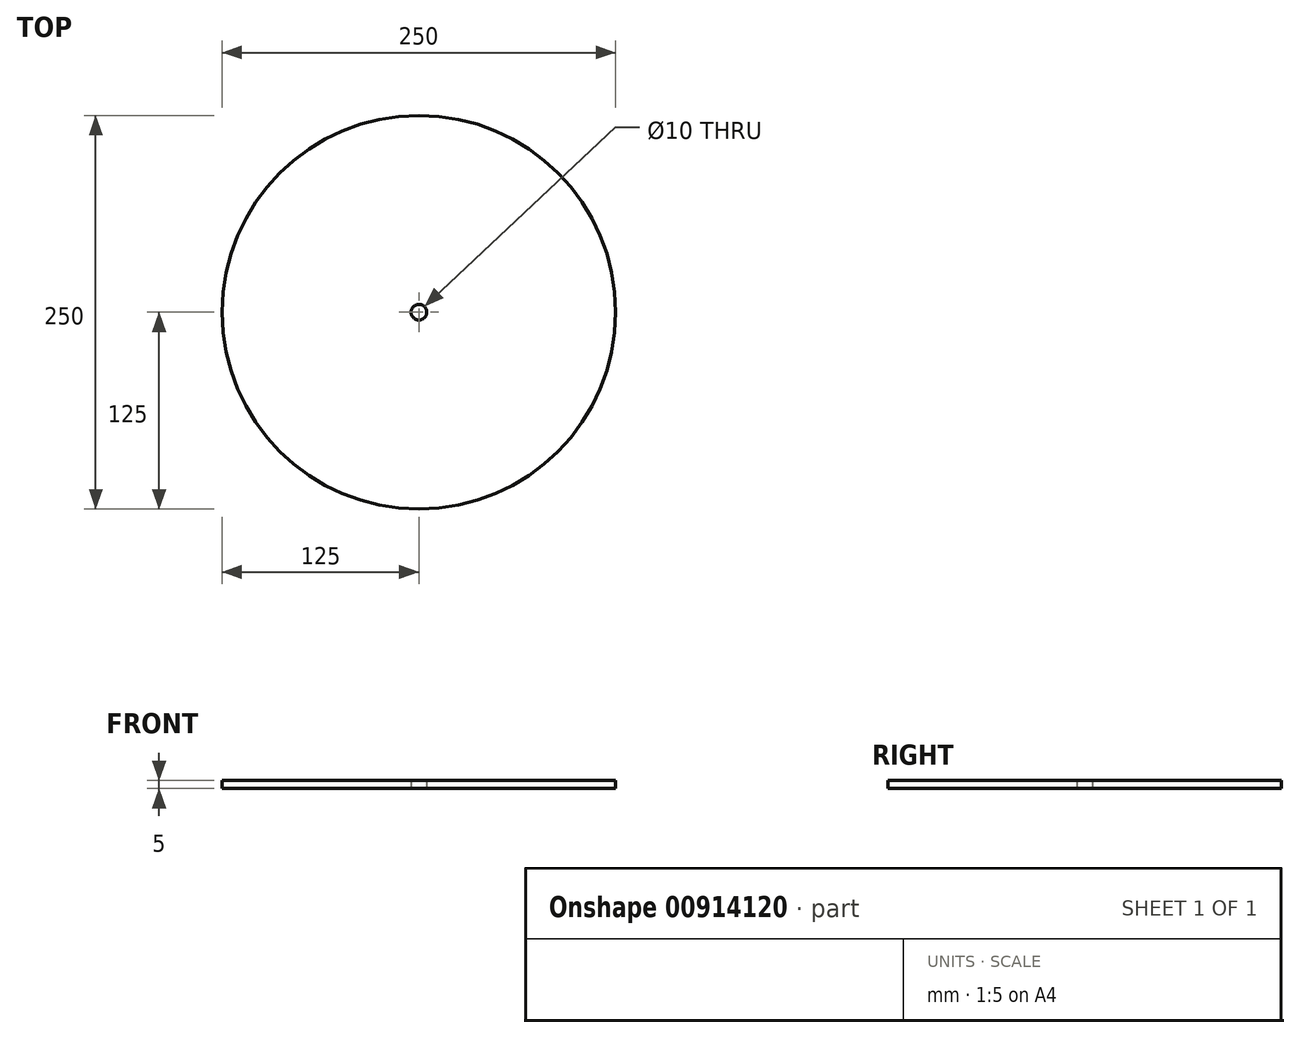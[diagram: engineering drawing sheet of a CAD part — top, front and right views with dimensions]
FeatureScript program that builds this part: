
annotation { "Feature Type Name" : "Feature", "Feature Type Description" : "" }
export const myFeature = defineFeature(function(context is Context, id is Id, definition is map)
    precondition{}
    {
        {
            var Q0;
            Q0=qCreatedBy(makeId("Top.planeOp"),FACE);
            var sketch = newSketch(context, id + "F0", { "sketchPlane" : qUnion([Q0])});
            skCircle(sketch, "E0", {"center": v(0, 0) * mm, "radius": 125 * mm});
            skCircle(sketch, "E1", {"center": v(0, 0) * mm, "radius": 5 * mm});
            skSolve(sketch);
        }
        {
            var Q0;
            Q0=makeQuery(id+"F0.imprint","IMPRINT",FACE,{"disambiguationData":[TD([[makeQuery(id+"F0.imprint","IMPRINT",EDGE,{"derivedFrom":sQuery(id+"F0.wireOp",EDGE,"E0")}),1.0]])]});
            extrude(context, id + "F1", {"entities" : qUnion([Q0]), "depth" : 5 * mm, "offsetDistance" : 25 * mm});
        }
    });
